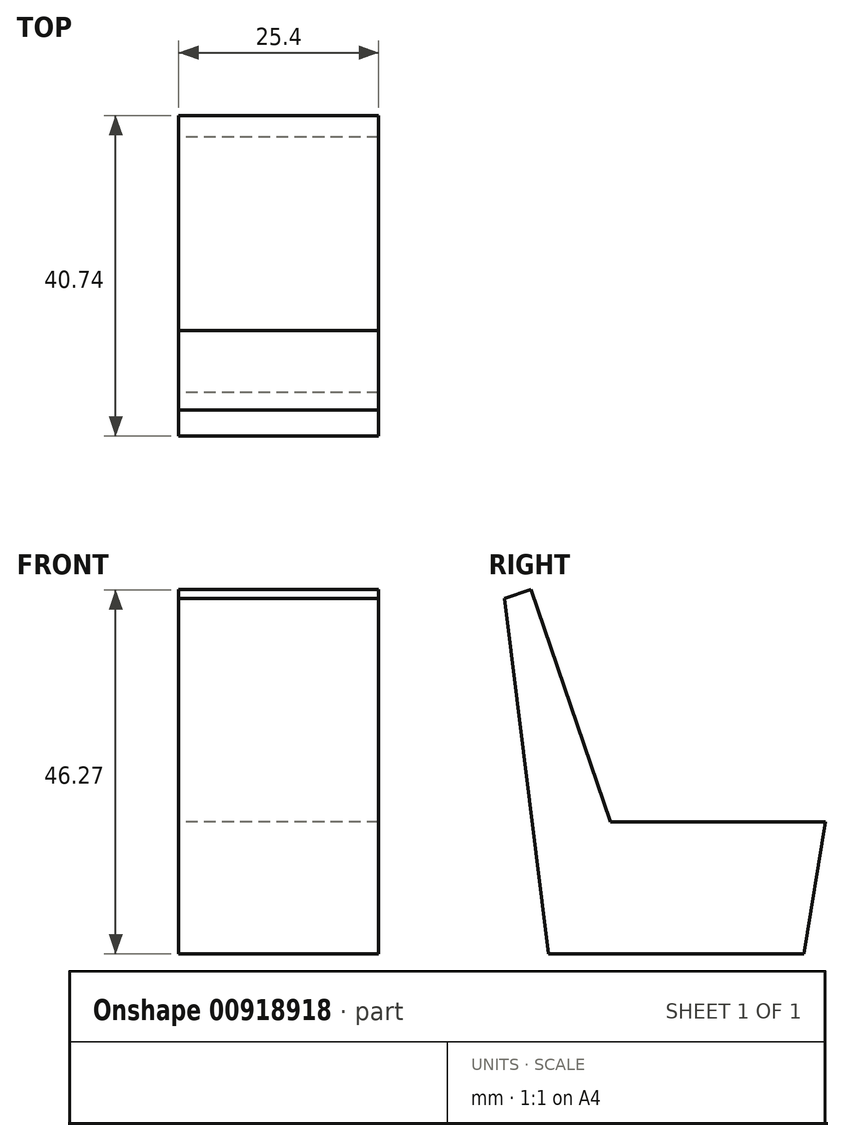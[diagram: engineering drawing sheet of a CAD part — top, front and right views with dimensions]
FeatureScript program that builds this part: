
annotation { "Feature Type Name" : "Feature", "Feature Type Description" : "" }
export const myFeature = defineFeature(function(context is Context, id is Id, definition is map)
    precondition{}
    {
        {
            var Q0;
            Q0=qCreatedBy(makeId("Right.planeOp"),FACE);
            var sketch = newSketch(context, id + "F0", { "sketchPlane" : qUnion([Q0])});
            skLineSegment(sketch, "E0", {"start": v(-17.8, 32.9) * mm, "end": v(-12.26, -12.26) * mm});
            skLineSegment(sketch, "E1", {"start": v(-12.26, -12.26) * mm, "end": v(20.19, -12.26) * mm});
            skLineSegment(sketch, "E2", {"start": v(20.19, -12.26) * mm, "end": v(22.95, 4.52) * mm});
            skLineSegment(sketch, "E3", {"start": v(22.95, 4.52) * mm, "end": v(-4.33, 4.52) * mm});
            skLineSegment(sketch, "E4", {"start": v(-4.33, 4.52) * mm, "end": v(-14.47, 34.01) * mm});
            skLineSegment(sketch, "E5", {"start": v(-14.47, 34.01) * mm, "end": v(-17.8, 32.9) * mm});
            skSolve(sketch);
        }
        {
            var Q0;
            Q0 = qSketchRegion(id + "F0", true);
            extrude(context, id + "F1", {"entities" : qUnion([Q0]), "depth" : 25.4 * mm, "offsetDistance" : 25.4 * mm});
        }
    });
